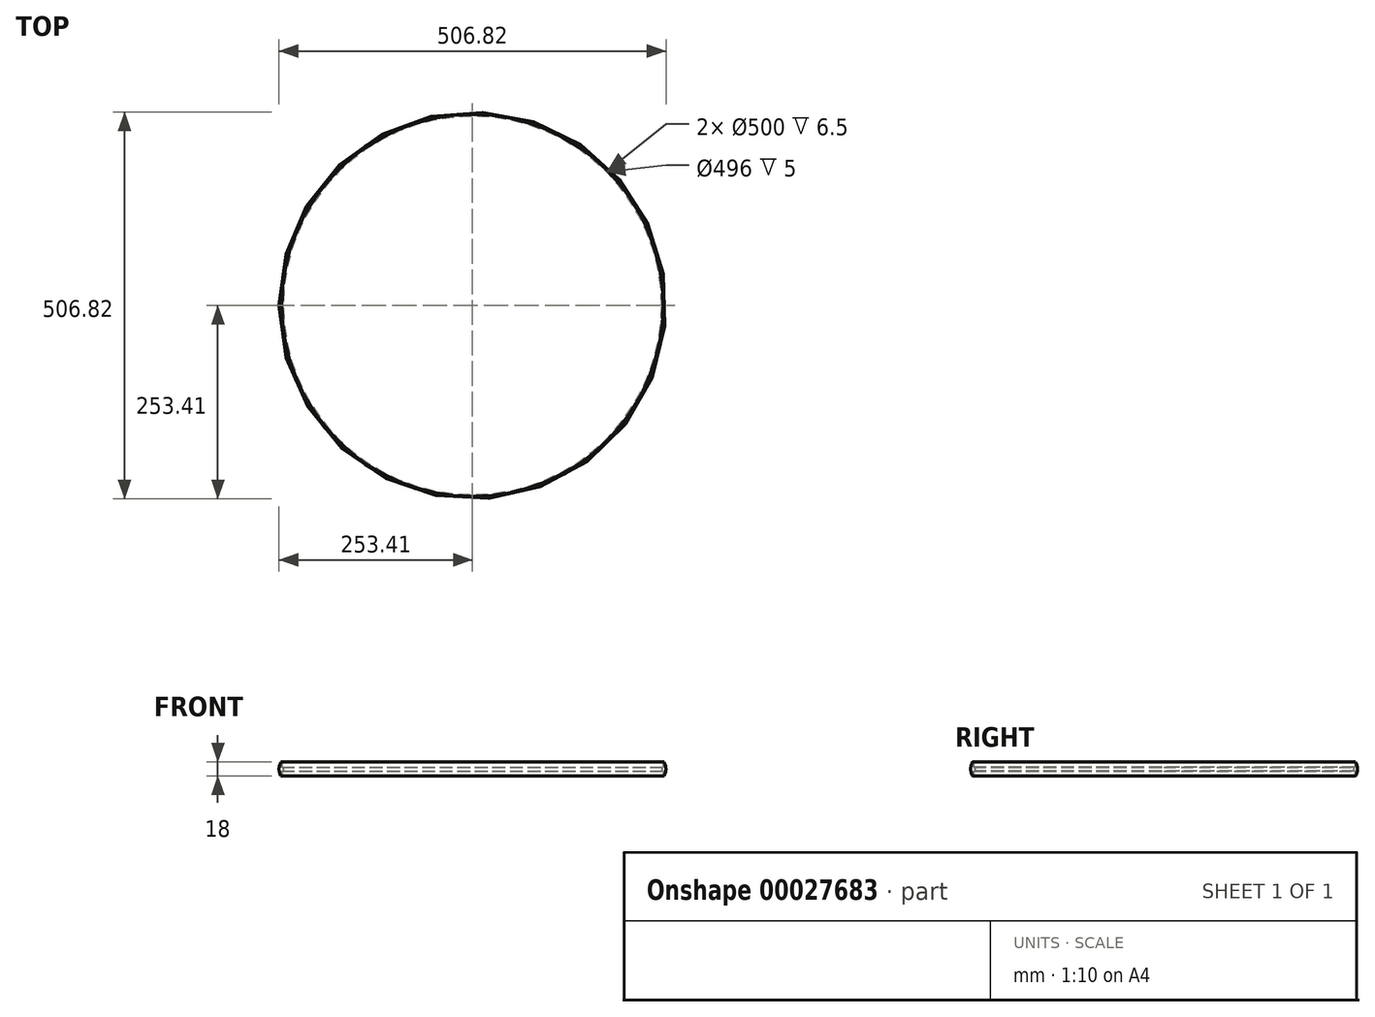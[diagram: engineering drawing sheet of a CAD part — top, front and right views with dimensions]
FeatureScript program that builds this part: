
annotation { "Feature Type Name" : "Feature", "Feature Type Description" : "" }
export const myFeature = defineFeature(function(context is Context, id is Id, definition is map)
    precondition{}
    {
        {
            var Q0;
            Q0=qCreatedBy(makeId("Front.planeOp"),FACE);
            var sketch = newSketch(context, id + "F0", { "sketchPlane" : qUnion([Q0])});
            skLineSegment(sketch, "E0", {"start": v(0, 0) * mm, "end": v(-250, 0) * mm});
            skLineSegment(sketch, "E1", {"start": v(0, 0) * mm, "end": v(0, 18) * mm});
            skLineSegment(sketch, "E2", {"start": v(0, 18) * mm, "end": v(-250, 18) * mm});
            skLineSegment(sketch, "E3", {"start": v(-250, 18) * mm, "end": v(-250, 11.5) * mm});
            skLineSegment(sketch, "E4", {"start": v(-250, 11.5) * mm, "end": v(-248, 11.5) * mm});
            skLineSegment(sketch, "E5", {"start": v(-248, 11.5) * mm, "end": v(-248, 6.5) * mm});
            skLineSegment(sketch, "E6", {"start": v(-248, 6.5) * mm, "end": v(-250, 6.5) * mm});
            skLineSegment(sketch, "E7.trimOffspring", {"start": v(-250, 6.5) * mm, "end": v(-250, 0) * mm});
            skSolve(sketch);
        }
        {
            var Q0;
            Q0=makeQuery(id+"F0.imprint","IMPRINT",FACE,{"disambiguationData":[TD([[makeQuery(id+"F0.imprint","IMPRINT",EDGE,{"derivedFrom":sQuery(id+"F0.wireOp",EDGE,"E0")}),-1.0]])]});
            var Q1;
            Q1=sQuery(id+"F0.wireOp",EDGE,"E1");
            revolve(context, id + "F1", {"entities" : qUnion([Q0]), "axis" : qUnion([Q1]), "revolveType" : RevolveType.FULL});
        }
        {
            var Q0;
            Q0=qCreatedBy(makeId("Front.planeOp"),FACE);
            var sketch = newSketch(context, id + "F3", { "sketchPlane" : qUnion([Q0])});
            skLineSegment(sketch, "E8", {"start": v(-248, 6.5) * mm, "end": v(-248, 11.5) * mm});
            skLineSegment(sketch, "E9", {"start": v(248, 11.5) * mm, "end": v(248, 6.5) * mm});
            skLineSegment(sketch, "E10.0", {"start": v(250, 11.5) * mm, "end": v(248, 11.5) * mm});
            skLineSegment(sketch, "E11", {"start": v(-250, 0) * mm, "end": v(-250, 6.5) * mm});
            skLineSegment(sketch, "E12", {"start": v(250, 6.5) * mm, "end": v(250, 0) * mm});
            skLineSegment(sketch, "E13", {"start": v(-250, 11.5) * mm, "end": v(-250, 18) * mm});
            skLineSegment(sketch, "E14", {"start": v(250, 18) * mm, "end": v(250, 11.5) * mm});
            skLineSegment(sketch, "E15.0", {"start": v(250, 6.5) * mm, "end": v(248, 6.5) * mm});
            skLineSegment(sketch, "E16.trimOffspring", {"start": v(-248, 6.5) * mm, "end": v(-250, 6.5) * mm});
            skLineSegment(sketch, "E17.trimOffspring", {"start": v(-248, 11.5) * mm, "end": v(-250, 11.5) * mm});
            skLineSegment(sketch, "E18", {"start": v(-250, 18) * mm, "end": v(-251, 18) * mm});
            skLineSegment(sketch, "E19", {"start": v(-250, 0) * mm, "end": v(-251, 0) * mm});
            skArc(sketch, "E20", {"start": v(-251, 18) * mm, "mid": v(-253.41, 9) * mm, "end": v(-251, 0) * mm});
            skLineSegment(sketch, "E21", {"start": v(0, 0) * mm, "end": v(0, 18) * mm, "construction": true});
            skSolve(sketch);
        }
        {
            var Q0;
            Q0=makeQuery(id+"F3.imprint","IMPRINT",FACE,{"disambiguationData":[TD([[makeQuery(id+"F3.imprint","IMPRINT",EDGE,{"derivedFrom":sQuery(id+"F3.wireOp",EDGE,"E8")}),1.0]])]});
            var Q1;
            Q1=sQuery(id+"F3.wireOp",EDGE,"E21");
            revolve(context, id + "F2", {"entities" : qUnion([Q0]), "axis" : qUnion([Q1]), "revolveType" : RevolveType.FULL});
        }
    });
